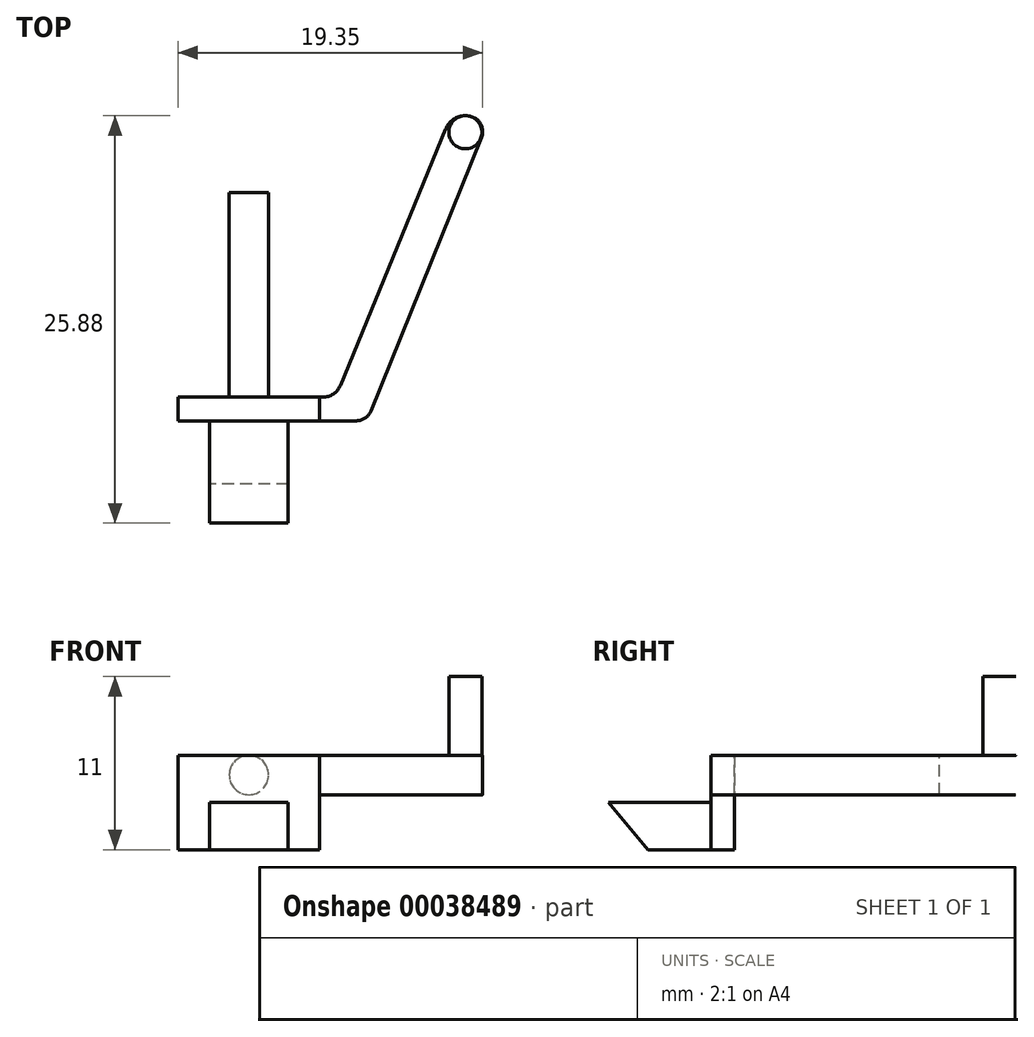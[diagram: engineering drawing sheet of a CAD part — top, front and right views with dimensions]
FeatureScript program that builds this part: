
annotation { "Feature Type Name" : "Feature", "Feature Type Description" : "" }
export const myFeature = defineFeature(function(context is Context, id is Id, definition is map)
    precondition{}
    {
        {
            var Q0;
            Q0=qCreatedBy(makeId("Front.planeOp"),FACE);
            var sketch = newSketch(context, id + "F0", { "sketchPlane" : qUnion([Q0])});
            skLineSegment(sketch, "E0.bottom", {"start": v(0, 0) * mm, "end": v(9, 0) * mm});
            skLineSegment(sketch, "E0.top", {"start": v(0, 6) * mm, "end": v(9, 6) * mm});
            skLineSegment(sketch, "E0.left", {"start": v(0, 0) * mm, "end": v(0, 6) * mm});
            skLineSegment(sketch, "E0.right", {"start": v(9, 0) * mm, "end": v(9, 6) * mm});
            skSolve(sketch);
        }
        {
            var Q0;
            Q0=makeQuery(id+"F0.imprint","IMPRINT",FACE,{"disambiguationData":[TD([[makeQuery(id+"F0.imprint","IMPRINT",EDGE,{"derivedFrom":sQuery(id+"F0.wireOp",EDGE,"E0.bottom")}),1.0]])]});
            extrude(context, id + "F1", {"entities" : qUnion([Q0]), "depth" : 1.5 * mm});
        }
        {
            var Q0;
            Q0=qCreatedBy(makeId("Right.planeOp"),FACE);
            cPlane(context, id + "F2", {"entities" : qUnion([Q0]), "cplaneType" : CPlaneType.OFFSET, "offset" : 4.5 * mm, "width" : 150 * mm, "height" : 150 * mm});
        }
        {
            var Q0;
            Q0=qCreatedBy(id+"F2.planeOp",FACE);
            var sketch = newSketch(context, id + "F3", { "sketchPlane" : qUnion([Q0])});
            skLineSegment(sketch, "E1.0", {"start": v(-1.5, 0) * mm, "end": v(-1.5, 6) * mm});
            skLineSegment(sketch, "E1.1", {"start": v(-1.5, 0) * mm, "end": v(0, 0) * mm});
            skLineSegment(sketch, "E2", {"start": v(-1.5, 0) * mm, "end": v(-5.5, 0) * mm});
            skLineSegment(sketch, "E3", {"start": v(-5.5, 0) * mm, "end": v(-8, 3) * mm});
            skLineSegment(sketch, "E4", {"start": v(-8, 3) * mm, "end": v(-1.5, 3) * mm});
            skLineSegment(sketch, "E5", {"start": v(-1.5, 3) * mm, "end": v(-1.5, 0) * mm});
            skSolve(sketch);
        }
        {
            var Q0;
            Q0=makeQuery(id+"F3.imprint","IMPRINT",FACE,{"disambiguationData":[TD([[makeQuery(id+"F3.imprint","IMPRINT",EDGE,{"derivedFrom":sQuery(id+"F3.wireOp",EDGE,"E2")}),-1.0]])]});
            extrude(context, id + "F4", {"entities" : qUnion([Q0]), "operationType" : NewBodyOperationType.ADD, "endBound" : BoundingType.SYMMETRIC, "depth" : 5 * mm});
        }
        {
            var Q0;
            Q0=makeQuery(id+"F1.opExtrude","SWEPT_FACE",FACE,{"disambiguationData":[OSD([sQuery(id+"F0.wireOp",EDGE,"E0.top")])]});
            var sketch = newSketch(context, id + "F5", { "sketchPlane" : qUnion([Q0])});
            skLineSegment(sketch, "E6.0", {"start": v(9, -1.5) * mm, "end": v(9, 0) * mm});
            skLineSegment(sketch, "E7", {"start": v(9, -1.5) * mm, "end": v(12, -1.5) * mm});
            skLineSegment(sketch, "E8", {"start": v(12, -1.5) * mm, "end": v(19.5, 17.04) * mm});
            skLineSegment(sketch, "E9", {"start": v(9, 0) * mm, "end": v(9.2, 0) * mm});
            skLineSegment(sketch, "E10", {"start": v(10.3, 0.74) * mm, "end": v(17, 17.04) * mm});
            skArc(sketch, "E11", {"start": v(19.5, 17.04) * mm, "mid": v(18.25, 17.88) * mm, "end": v(17, 17.04) * mm});
            skPoint(sketch, "E12.visualSharp", {"position": v(10, 0) * mm});
            skArc(sketch, "E12.filletArc", {"start": v(9.2, 0) * mm, "mid": v(9.86, 0.2) * mm, "end": v(10.3, 0.74) * mm});
            skSolve(sketch);
        }
        {
            var Q0;
            Q0 = qSketchRegion(id + "F5", true);
            extrude(context, id + "F6", {"entities" : qUnion([Q0]), "oppositeDirection" : true, "depth" : 2.5 * mm});
        }
        {
            var Q0;
            Q0=makeQuery(id+"F6.opExtrude","SWEPT_EDGE",EDGE,{"disambiguationData":[OSD([sQuery(id+"F5.wireOp",EDGE,"E7"),sQuery(id+"F5.wireOp",EDGE,"E8")])]});
            fillet(context, id + "F7", {"entities" : qUnion([Q0]), "radius" : 1 * mm, "tangentPropagation" : true, "allowEdgeOverflow" : false});
        }
        {
            var Q0;
            Q0=makeQuery(id+"F6.opExtrude","CAP_FACE",FACE,{"disambiguationData":[OSD([sQuery(id+"F5.wireOp",EDGE,"E6.0"),sQuery(id+"F5.wireOp",EDGE,"E7"),sQuery(id+"F5.wireOp",EDGE,"E8"),sQuery(id+"F5.wireOp",EDGE,"E9"),sQuery(id+"F5.wireOp",EDGE,"E10"),sQuery(id+"F5.wireOp",EDGE,"E11"),sQuery(id+"F5.wireOp",EDGE,"E12.filletArc")])],"isStart":true});
            var sketch = newSketch(context, id + "F8", { "sketchPlane" : qUnion([Q0])});
            skCircle(sketch, "E13", {"center": v(18.25, 16.83) * mm, "radius": 1.05 * mm});
            skPoint(sketch, "E13.centerSnap0", {"position": v(18.25, 17.88) * mm});
            skSolve(sketch);
        }
        {
            var Q0;
            Q0=makeQuery(id+"F8.imprint","IMPRINT",FACE,{"disambiguationData":[TD([[makeQuery(id+"F8.imprint","IMPRINT",EDGE,{"derivedFrom":sQuery(id+"F8.wireOp",EDGE,"E13")}),1.0]])]});
            extrude(context, id + "F9", {"entities" : qUnion([Q0]), "operationType" : NewBodyOperationType.ADD, "depth" : 5 * mm});
        }
        {
            var Q0;
            Q0=makeQuery(id+"F0.imprint","IMPRINT",FACE,{"disambiguationData":[TD([[makeQuery(id+"F0.imprint","IMPRINT",EDGE,{"derivedFrom":sQuery(id+"F0.wireOp",EDGE,"E0.bottom")}),1.0]])]});
            var sketch = newSketch(context, id + "F10", { "sketchPlane" : qUnion([Q0])});
            skLineSegment(sketch, "E14.0", {"start": v(0, 6) * mm, "end": v(9, 6) * mm});
            skLineSegment(sketch, "E15", {"start": v(4.5, 6) * mm, "end": v(4.5, 0) * mm, "construction": true});
            skCircle(sketch, "E16", {"center": v(4.5, 4.75) * mm, "radius": 1.25 * mm});
            skSolve(sketch);
        }
        {
            var Q0;
            Q0=makeQuery(id+"F10.imprint","IMPRINT",FACE,{"disambiguationData":[TD([[makeQuery(id+"F10.imprint","IMPRINT",EDGE,{"derivedFrom":sQuery(id+"F10.wireOp",EDGE,"E16")}),1.0]])]});
            extrude(context, id + "F11", {"entities" : qUnion([Q0]), "operationType" : NewBodyOperationType.ADD, "oppositeDirection" : true, "depth" : 13 * mm});
        }
        {
            var Q0;
            Q0=makeQuery(id+"F6.opExtrude","SWEPT_EDGE",EDGE,{"disambiguationData":[OSD([sQuery(id+"F5.wireOp",EDGE,"E8"),sQuery(id+"F5.wireOp",EDGE,"E11")])]});
            fillet(context, id + "F12", {"entities" : qUnion([Q0]), "radius" : 1 * mm, "tangentPropagation" : true, "allowEdgeOverflow" : false});
        }
    });
